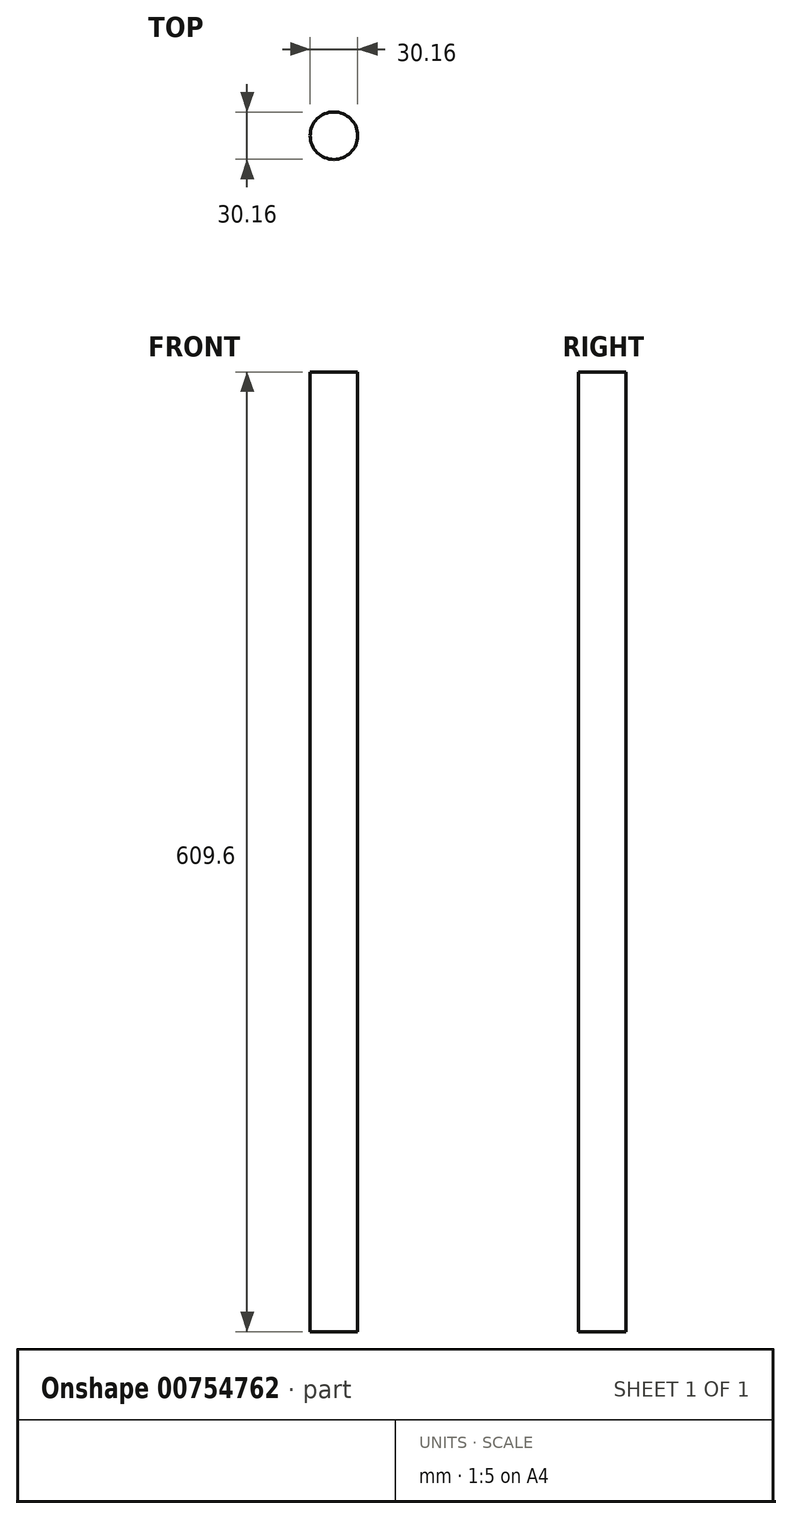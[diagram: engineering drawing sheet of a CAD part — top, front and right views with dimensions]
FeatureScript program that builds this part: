
annotation { "Feature Type Name" : "Feature", "Feature Type Description" : "" }
export const myFeature = defineFeature(function(context is Context, id is Id, definition is map)
    precondition{}
    {
        {
            var Q0;
            Q0=qCreatedBy(makeId("Top.planeOp"),FACE);
            cPlane(context, id + "F0", {"entities" : qUnion([Q0]), "cplaneType" : CPlaneType.OFFSET, "offset" : 31.75 * mm, "width" : 152.4 * mm, "height" : 152.4 * mm});
        }
        {
            var Q0;
            Q0=qCreatedBy(id+"F0.planeOp",FACE);
            var sketch = newSketch(context, id + "F1", { "sketchPlane" : qUnion([Q0])});
            skCircle(sketch, "E0", {"center": v(0, 0) * mm, "radius": 15.08 * mm});
            skSolve(sketch);
        }
        {
            var Q0;
            Q0=qSketchRegion(id+"F1",true);
            extrude(context, id + "F2", {"entities" : qUnion([Q0]), "oppositeDirection" : true, "depth" : 609.6 * mm, "offsetDistance" : 25.4 * mm});
        }
    });
